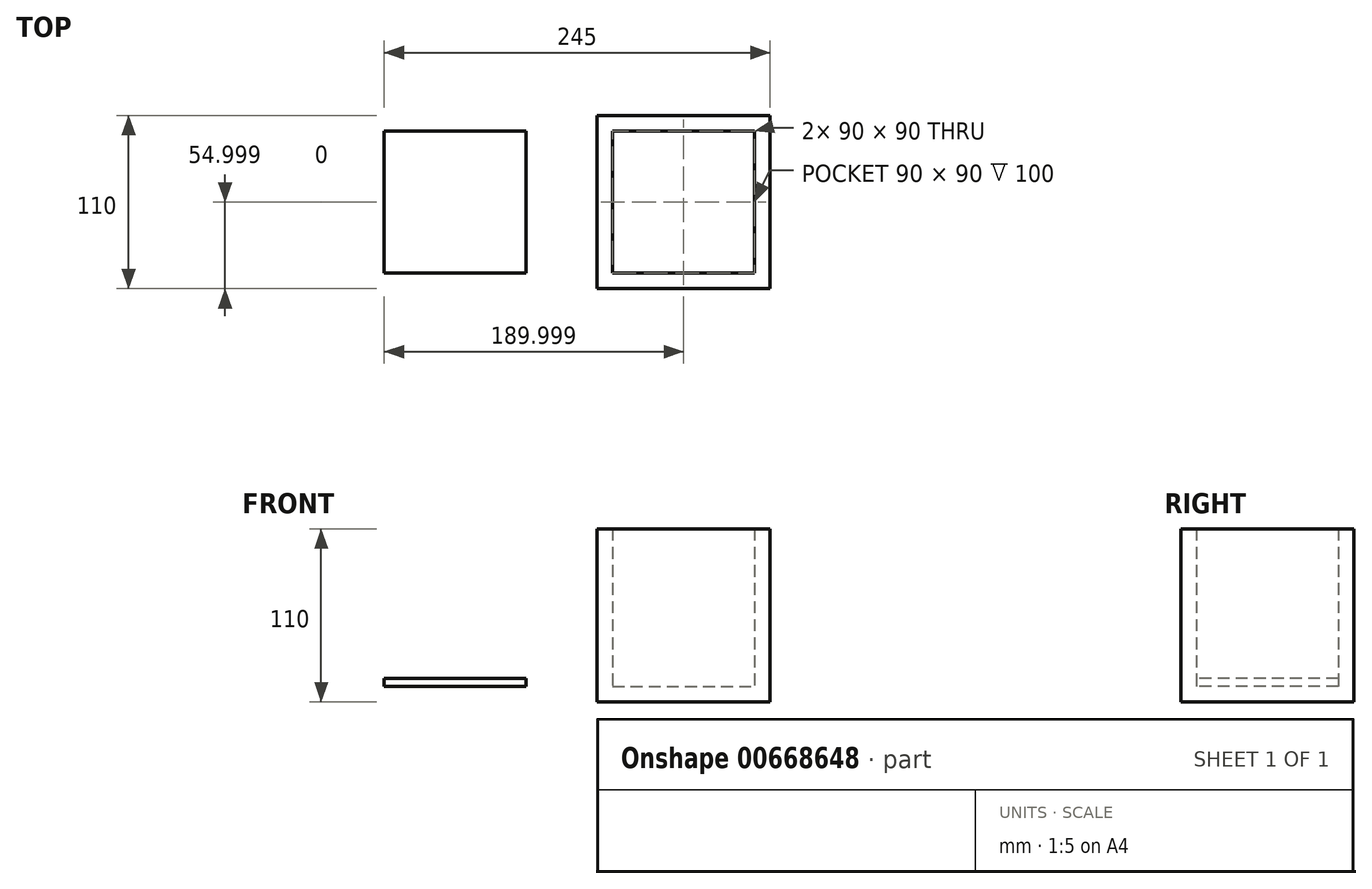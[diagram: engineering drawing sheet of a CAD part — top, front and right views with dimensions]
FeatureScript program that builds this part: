
annotation { "Feature Type Name" : "Feature", "Feature Type Description" : "" }
export const myFeature = defineFeature(function(context is Context, id is Id, definition is map)
    precondition{}
    {
        {
            var Q0;
            Q0=qCreatedBy(makeId("Top.planeOp"),FACE);
            var sketch = newSketch(context, id + "F0", { "sketchPlane" : qUnion([Q0])});
            skLineSegment(sketch, "E0.bottom", {"start": v(-125.27, 23.08) * mm, "end": v(-15.27, 23.08) * mm});
            skLineSegment(sketch, "E0.top", {"start": v(-125.27, -86.92) * mm, "end": v(-15.27, -86.92) * mm});
            skLineSegment(sketch, "E0.left", {"start": v(-125.27, 23.08) * mm, "end": v(-125.27, -86.92) * mm});
            skLineSegment(sketch, "E0.right", {"start": v(-15.27, 23.08) * mm, "end": v(-15.27, -86.92) * mm});
            skSolve(sketch);
        }
        {
            var Q0;
            Q0 = qSketchRegion(id + "F0", true);
            extrude(context, id + "F1", {"entities" : qUnion([Q0]), "depth" : 110 * mm, "offsetDistance" : 25 * mm});
        }
        {
            var Q0;
            Q0=makeQuery(id+"F1.opExtrude","CAP_FACE",FACE,{"disambiguationData":[OSD([sQuery(id+"F0.wireOp",EDGE,"E0.bottom"),sQuery(id+"F0.wireOp",EDGE,"E0.top"),sQuery(id+"F0.wireOp",EDGE,"E0.left"),sQuery(id+"F0.wireOp",EDGE,"E0.right")])],"isStart":false});
            shell(context, id + "F2", {"entities" : qUnion([Q0]), "thickness" : 10 * mm});
        }
        {
            var Q0;
            Q0=makeQuery(id+"F2.opShell","OFFSET_FACE",FACE,{"disambiguationData":[OSD([sQuery(id+"F0.wireOp",EDGE,"E0.bottom"),sQuery(id+"F0.wireOp",EDGE,"E0.top"),sQuery(id+"F0.wireOp",EDGE,"E0.left"),sQuery(id+"F0.wireOp",EDGE,"E0.right")])]});
            extrude(context, id + "F3", {"entities" : qUnion([Q0]), "depth" : 5 * mm, "offsetDistance" : 25 * mm});
        }
        {
            var Q0;
            Q0=makeQuery(id+"F3.opExtrude","SWEPT_BODY",BODY,{"disambiguationData":[OSD([sQuery(id+"F0.wireOp",EDGE,"E0.bottom"),sQuery(id+"F0.wireOp",EDGE,"E0.top"),sQuery(id+"F0.wireOp",EDGE,"E0.left"),sQuery(id+"F0.wireOp",EDGE,"E0.right")])]});
            transform(context, id + "F4", {"entities" : qUnion([Q0]), "transformType" : TransformType.TRANSLATION_3D, "dx" : -145 * mm, "dy" : 0 * mm, "dz" : 0 * mm, "makeCopy" : false});
        }
    });
